# Revit family: oventrop_hydrocontrol-vgc_1063051-4055rfa
name_source: partatom
category: Арматура трубопроводов
revit_build: Autodesk Revit 2017 (Build: 20160225_1515(x64)
units: mm (PartAtom-declared; Revit-internal decimal feet)

## family parameters
Всегда вертикально = Да
Заголовок OmniClass = Adjusting/Controlling Valves for Liquid Services
На основе рабочей плоскости = Нет
Номер OmniClass = 23.65.55.14.17
Общий = Нет
При загрузке вырезать с полостями = Нет
Размер круглого соединителя = Использовать радиус
Тип детали = Клапан - Вставляется

## types (8) — shared parameters
Angle = 60.00°
Angle 3 = -60.00°
Article Description = Balancing valve with groove connection
Article Type = Hydrocontrol VGC 10630
Bonnet = Color RGB 35-35-35
Bonnet Radius = 80 мм
Bronze = Color RGB 156-122-90
Cast iron = Color RGB 140-140-140
Custom = Нет
EMCS Version = 2.0
ETIM Article Class = EC011463
Family Version = 10.14
Hb4 = 18 мм
Hb5 = 3 мм
Hlp1 = 22 мм
IFCExportAs = IfcValveType
IFCExportType = PRESSUREREDUCING
Lgt1 = 15.9 мм
Lgt2 = 8.7 мм
Lgt3 = 9 мм
MEPcontent Class = VALVE_BALANCING
Manufacturer URL = http://www.oventrop.de
Pressure Drop = 0.0 Па
Product Line = Oventrop
R1 = 9 мм
R2 = 10.39 мм
Revit Version = 2015
VDst = 21 мм
oAngle 2 = 30.00°
r1 = 2 мм
r2 = 3 мм
Группа модели = Hydrocontrol VGC 10630
Изготовитель = Oventrop
Описание = Balancing valve with groove connection

## per-type parameters (varying)
- DN 65-73 mm: CurDst=22.52 мм; Dst1=25.08 мм; DstChk=25.08 мм; GTIN=4026755225099; Hb1=187.75 мм; Hb2=75.24 мм; Hb3=18.81 мм; Hb6=78.37 мм; Height=200 мм; Hlp2=7.51 мм; L2=22.52 мм; Length=290 мм; Lgt4=108.2 мм; Manufacturer Art. No.=1063051; NominalDiameter=65.00 мм; OuterDiameter=73 мм; Rad1=36.5 мм; Rad2=34.4 мм; Rad3=42 мм; Rad4=39 мм; Rad5=51.5 мм; Rad6=41.5 мм; Rad7=53.5 мм; URL=www.stabiplan.com; VHth=49 мм
- DN 80-88.9 mm: CurDst=27.11 мм; Dst1=27.51 мм; DstChk=27.51 мм; GTIN=4026755225105; Hb1=205.07 мм; Hb2=87.97 мм; Hb3=21.99 мм; Hb6=92.15 мм; Height=215 мм; Hlp2=9.04 мм; L2=27.11 мм; Length=310 мм; Lgt4=114.8 мм; Manufacturer Art. No.=1063052; NominalDiameter=80.00 мм; OuterDiameter=88.9 мм; Rad1=44.45 мм; Rad2=42.35 мм; Rad3=49.95 мм; Rad4=46.95 мм; Rad5=59.45 мм; Rad6=49.45 мм; Rad7=61.45 мм; URL=www.stabiplan.com; VHth=56.95 мм
- DN 100-114.3 mm: CurDst=34.44 мм; Dst1=28.89 мм; DstChk=28.89 мм; GTIN=4026755225112; Hb1=238.56 мм; Hb2=114.12 мм; Hb3=28.53 мм; Hb6=120.46 мм; Height=244 мм; Hlp2=11.48 мм; L2=34.44 мм; Length=350 мм; Lgt4=128 мм; Manufacturer Art. No.=1063053; NominalDiameter=100.00 мм; OuterDiameter=114.3 мм; Rad1=57.15 мм; Rad2=55.05 мм; Rad3=62.65 мм; Rad4=59.65 мм; Rad5=72.15 мм; Rad6=62.15 мм; Rad7=74.15 мм; URL=www.stabiplan.com; VHth=69.65 мм
- DN 125-139.7 mm: CurDst=41.77 мм; Dst1=27.76 мм; DstChk=27.76 мм; GTIN=4026755231878; Hb1=290.52 мм; Hb2=158.75 мм; Hb3=39.69 мм; Hb6=168.77 мм; Height=289 мм; Hlp2=13.92 мм; L2=41.77 мм; Length=400 мм; Lgt4=144.5 мм; Manufacturer Art. No.=1064054; NominalDiameter=125.00 мм; OuterDiameter=139.7 мм; Rad1=69.85 мм; Rad2=67.75 мм; Rad3=75.35 мм; Rad4=72.35 мм; Rad5=90.35 мм; Rad6=80.35 мм; Rad7=92.35 мм; URL=www.stabiplan.com; VHth=82.35 мм
- DN 150-165.1 mm: CurDst=49.1 мм; Dst1=41.64 мм; DstChk=41.64 мм; GTIN=4026755231885; Hb1=295.14 мм; Hb2=156.04 мм; Hb3=39.01 мм; Hb6=165.84 мм; Height=293 мм; Hlp2=16.37 мм; L2=49.1 мм; Length=480 мм; Lgt4=170.9 мм; Manufacturer Art. No.=1064055; NominalDiameter=150.00 мм; OuterDiameter=165.1 мм; Rad1=82.55 мм; Rad2=80.45 мм; Rad3=88.05 мм; Rad4=85.05 мм; Rad5=103.05 мм; Rad6=93.05 мм; Rad7=105.05 мм; URL=www.stabiplan.com; VHth=95.05 мм
- DN 65-76.1 mm: CurDst=23.41 мм; Dst1=27.01 мм; DstChk=27.01 мм; GTIN=4026755231861; Hb1=187.75 мм; Hb2=74.34 мм; Hb3=18.59 мм; Hb6=77.4 мм; Height=200 мм; Hlp2=7.8 мм; L2=23.41 мм; Length=290 мм; Lgt4=108.2 мм; Manufacturer Art. No.=1064051; NominalDiameter=65.00 мм; OuterDiameter=76.1 мм; Rad1=38.05 мм; Rad2=35.95 мм; Rad3=43.55 мм; Rad4=40.55 мм; Rad5=53.05 мм; Rad6=43.05 мм; Rad7=55.05 мм; URL=http://file-system.ru; VHth=50.55 мм
- DN 125-141.3 mm: CurDst=42.23 мм; Dst1=28.76 мм; DstChk=28.76 мм; GTIN=4026755225129; Hb1=290.52 мм; Hb2=158.29 мм; Hb3=39.57 мм; Hb6=168.27 мм; Height=289 мм; Hlp2=14.08 мм; L2=42.23 мм; Length=400 мм; Lgt4=144.5 мм; Manufacturer Art. No.=1063054; NominalDiameter=125.00 мм; OuterDiameter=141.3 мм; Rad1=70.65 мм; Rad2=68.55 мм; Rad3=76.15 мм; Rad4=73.15 мм; Rad5=91.15 мм; Rad6=81.15 мм; Rad7=93.15 мм; URL=www.stabiplan.com; VHth=83.15 мм
- DN 150-168.3 mm: CurDst=50.03 мм; Dst1=43.64 мм; DstChk=43.64 мм; GTIN=4026755225136; Hb1=295.14 мм; Hb2=155.11 мм; Hb3=38.78 мм; Hb6=164.84 мм; Height=293 мм; Hlp2=16.68 мм; L2=50.03 мм; Length=480 мм; Lgt4=170.9 мм; Manufacturer Art. No.=1063055; NominalDiameter=150.00 мм; OuterDiameter=168.3 мм; Rad1=84.15 мм; Rad2=82.05 мм; Rad3=89.65 мм; Rad4=86.65 мм; Rad5=104.65 мм; Rad6=94.65 мм; Rad7=106.65 мм; URL=www.stabiplan.com; VHth=96.65 мм

## geometry (parser evidence)
native form markers: Blend x2, Sweep x2
no freeform markers — native parametric forms only
